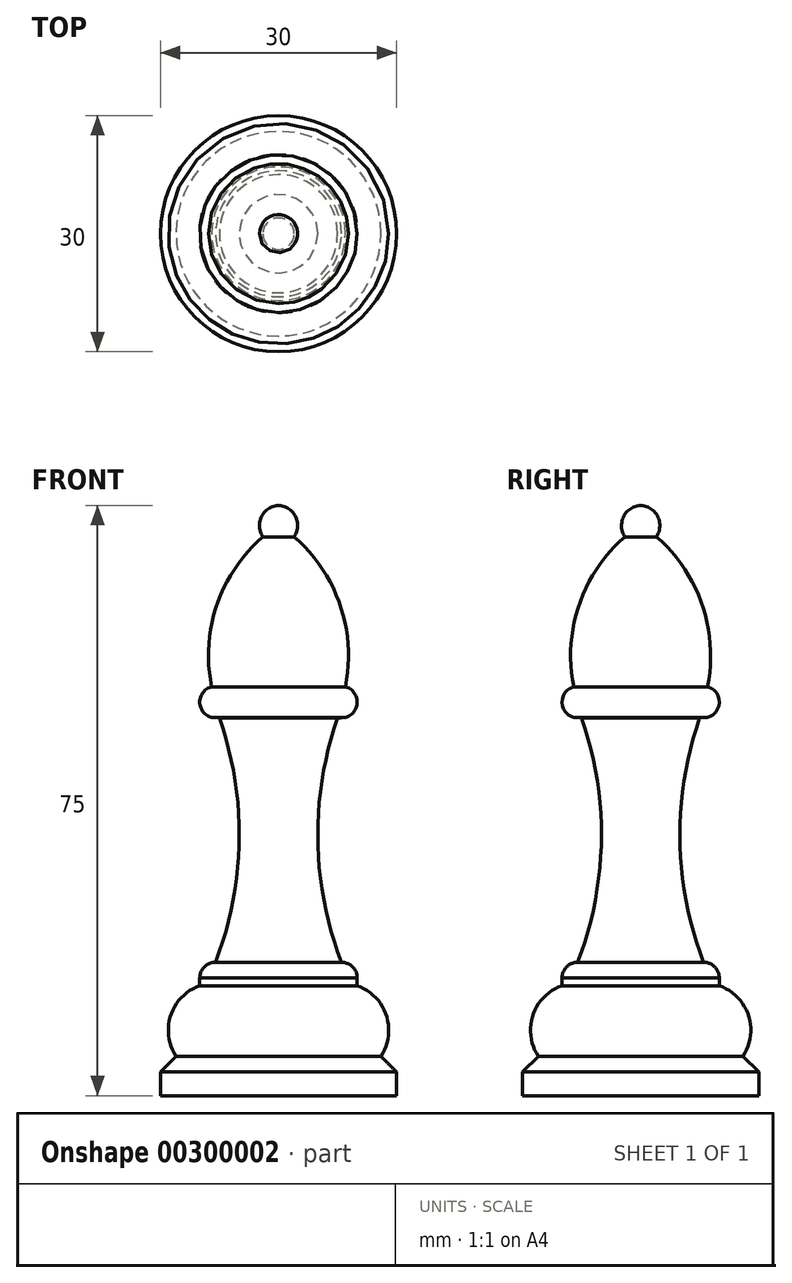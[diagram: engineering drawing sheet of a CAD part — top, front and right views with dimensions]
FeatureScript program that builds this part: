
annotation { "Feature Type Name" : "Feature", "Feature Type Description" : "" }
export const myFeature = defineFeature(function(context is Context, id is Id, definition is map)
    precondition{}
    {
        {
            var Q0;
            Q0=qCreatedBy(makeId("Front.planeOp"),FACE);
            var sketch = newSketch(context, id + "F0", { "sketchPlane" : qUnion([Q0])});
            skArc(sketch, "E0", {"start": v(8.5, -23.06) * mm, "mid": v(7.82, -12.65) * mm, "end": v(2, -4) * mm});
            skLineSegment(sketch, "E1", {"start": v(0, 0) * mm, "end": v(0, -75) * mm});
            skArc(sketch, "E2", {"start": v(10, -60.03) * mm, "mid": v(9.4, -58.63) * mm, "end": v(8, -58.05) * mm});
            skLineSegment(sketch, "E3", {"start": v(10, -60.03) * mm, "end": v(10, -61.03) * mm});
            skArc(sketch, "E4", {"start": v(13, -70) * mm, "mid": v(13.69, -64.78) * mm, "end": v(10, -61.03) * mm});
            skLineSegment(sketch, "E5", {"start": v(13, -70) * mm, "end": v(15, -72) * mm});
            skLineSegment(sketch, "E6", {"start": v(15, -72) * mm, "end": v(15, -75) * mm});
            skArc(sketch, "E7", {"start": v(7.5, -27.03) * mm, "mid": v(5, -42.59) * mm, "end": v(8, -58.05) * mm});
            skArc(sketch, "E8", {"start": v(8.5, -26.93) * mm, "mid": v(10, -25) * mm, "end": v(8.5, -23.06) * mm});
            skLineSegment(sketch, "E9", {"start": v(8.5, -26.93) * mm, "end": v(7.5, -27.03) * mm});
            skLineSegment(sketch, "E10", {"start": v(15, -75) * mm, "end": v(0, -75) * mm});
            skArc(sketch, "E11", {"start": v(2, -4) * mm, "mid": v(2.16, -1.42) * mm, "end": v(0, 0) * mm});
            skSolve(sketch);
        }
        {
            var Q0;
            Q0=makeQuery(id+"F0.imprint","IMPRINT",FACE,{"disambiguationData":[TD([[makeQuery(id+"F0.imprint","IMPRINT",EDGE,{"derivedFrom":sQuery(id+"F0.wireOp",EDGE,"E0")}),1.0]])]});
            var Q1;
            Q1=sQuery(id+"F0.wireOp",EDGE,"E1");
            revolve(context, id + "F1", {"entities" : qUnion([Q0]), "axis" : qUnion([Q1]), "revolveType" : RevolveType.FULL});
        }
    });
